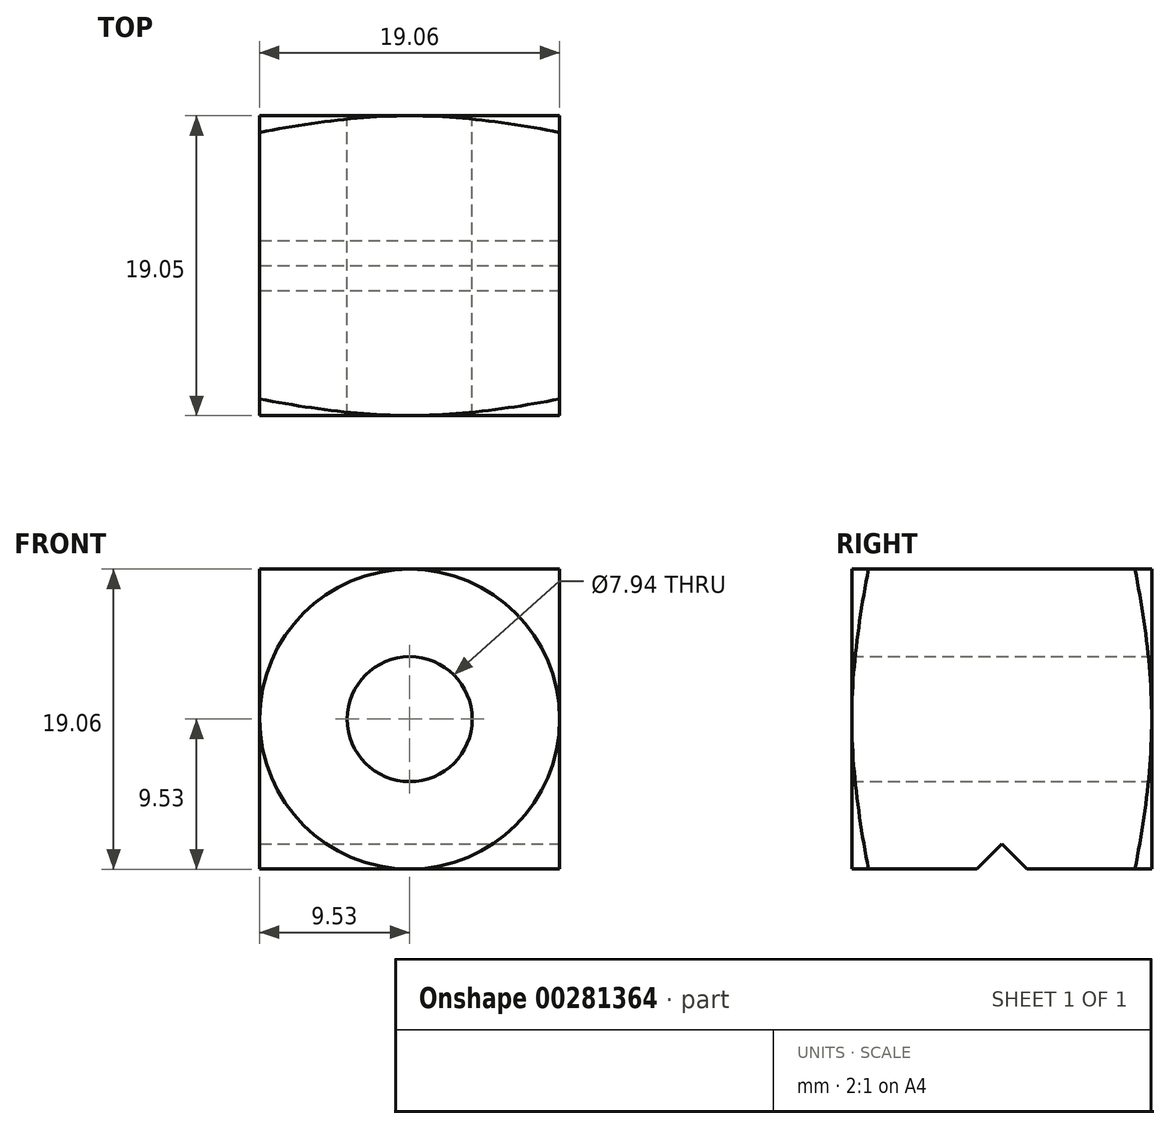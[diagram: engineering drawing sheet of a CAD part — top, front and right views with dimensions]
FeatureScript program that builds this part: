
annotation { "Feature Type Name" : "Feature", "Feature Type Description" : "" }
export const myFeature = defineFeature(function(context is Context, id is Id, definition is map)
    precondition{}
    {
        {
            var Q0;
            Q0=qCreatedBy(makeId("Front.planeOp"),FACE);
            var sketch = newSketch(context, id + "F0", { "sketchPlane" : qUnion([Q0])});
            skLineSegment(sketch, "E0.bottom", {"start": v(-9.52, -9.52) * mm, "end": v(9.52, -9.52) * mm});
            skLineSegment(sketch, "E0.top", {"start": v(-9.53, 9.52) * mm, "end": v(9.53, 9.52) * mm});
            skLineSegment(sketch, "E0.left", {"start": v(-9.53, -9.52) * mm, "end": v(-9.53, 9.52) * mm});
            skLineSegment(sketch, "E0.right", {"start": v(9.53, -9.52) * mm, "end": v(9.53, 9.52) * mm});
            skPoint(sketch, "E0.middle", {"position": v(0, 0) * mm});
            skCircle(sketch, "E1", {"center": v(0, 0) * mm, "radius": 3.97 * mm});
            skCircle(sketch, "E2", {"center": v(0, 0) * mm, "radius": 9.53 * mm});
            skSolve(sketch);
        }
        {
            var Q0;
            Q0 = qSketchRegion(id + "F0", true);
            extrude(context, id + "F1", {"entities" : qUnion([Q0]), "depth" : 19.05 * mm});
        }
        {
            var Q0;
            Q0=makeQuery(id+"F1.opExtrude","SWEPT_FACE",FACE,{"disambiguationData":[OSD([sQuery(id+"F0.wireOp",EDGE,"E0.right")])]});
            var sketch = newSketch(context, id + "F2", { "sketchPlane" : qUnion([Q0])});
            skLineSegment(sketch, "E3", {"start": v(-9.53, -7.94) * mm, "end": v(-11.11, -9.52) * mm});
            skPoint(sketch, "E3.startSnap0", {"position": v(-9.53, -9.52) * mm});
            skLineSegment(sketch, "E4", {"start": v(-9.53, -7.94) * mm, "end": v(-7.94, -9.52) * mm});
            skLineSegment(sketch, "E5", {"start": v(-9.53, -7.94) * mm, "end": v(-9.53, -15.34) * mm, "construction": true});
            skSolve(sketch);
        }
        {
            var Q0;
            Q0 = qSketchRegion(id + "F2", true);
            var Q1;
            {var subQ0=sQuery(id+"F2.wireOp",EDGE,"E3");Q1=makeQuery(id+"F2.imprint","IMPRINT",FACE,{"disambiguationData":[TD([[makeQuery(id+"F2.imprint","IMPRINT",EDGE,{"derivedFrom":subQ0}),1.0]])]});}
            extrude(context, id + "F3", {"entities" : qUnion([Q0, Q1]), "operationType" : NewBodyOperationType.REMOVE, "oppositeDirection" : true, "depth" : 19.05 * mm});
        }
        {
            var Q0;
            Q0=makeQuery(id+"F1.opExtrude","SWEPT_FACE",FACE,{"disambiguationData":[OSD([sQuery(id+"F0.wireOp",EDGE,"E0.right")])]});
            var Q1;
            Q1=makeQuery(id+"F1.opExtrude","SWEPT_FACE",FACE,{"disambiguationData":[OSD([sQuery(id+"F0.wireOp",EDGE,"E0.left")])]});
            cPlane(context, id + "F4", {"entities" : qUnion([Q0, Q1]), "cplaneType" : CPlaneType.MID_PLANE, "offset" : 25.4 * mm, "width" : 152.4 * mm, "height" : 152.4 * mm});
        }
        {
            var Q0;
            Q0=qCreatedBy(id+"F4.planeOp",FACE);
            var sketch = newSketch(context, id + "F5", { "sketchPlane" : qUnion([Q0])});
            skLineSegment(sketch, "E6.0.0", {"start": v(-11.11, -9.52) * mm, "end": v(-9.53, -7.94) * mm});
            skLineSegment(sketch, "E6.0.1", {"start": v(-9.53, -7.94) * mm, "end": v(-7.94, -9.52) * mm});
            skLineSegment(sketch, "E6.0.2", {"start": v(-7.94, -9.52) * mm, "end": v(0, -9.52) * mm});
            skLineSegment(sketch, "E6.0.3", {"start": v(0, -9.52) * mm, "end": v(0, 9.52) * mm});
            skLineSegment(sketch, "E6.0.4", {"start": v(0, 9.52) * mm, "end": v(-19.05, 9.52) * mm});
            skLineSegment(sketch, "E6.0.5", {"start": v(-19.05, 9.52) * mm, "end": v(-19.05, -9.52) * mm});
            skLineSegment(sketch, "E6.0.6", {"start": v(-19.05, -9.52) * mm, "end": v(-11.11, -9.52) * mm});
            skLineSegment(sketch, "E7", {"start": v(-19.05, 9.52) * mm, "end": v(-19.05, 20.54) * mm});
            skLineSegment(sketch, "E8", {"start": v(-19.05, 20.54) * mm, "end": v(-16.1, 20.54) * mm});
            skLineSegment(sketch, "E9", {"start": v(-16.1, 20.54) * mm, "end": v(-19.05, 9.52) * mm});
            skLineSegment(sketch, "E10", {"start": v(0, 9.52) * mm, "end": v(0, 20.54) * mm});
            skLineSegment(sketch, "E11", {"start": v(0, 20.54) * mm, "end": v(-2.95, 20.54) * mm});
            skLineSegment(sketch, "E12", {"start": v(-2.95, 20.54) * mm, "end": v(0, 9.53) * mm});
            skSolve(sketch);
        }
        {
            var Q0;
            Q0=makeQuery(id+"F5.imprint","IMPRINT",FACE,{"disambiguationData":[TD([[makeQuery(id+"F5.imprint","IMPRINT",EDGE,{"derivedFrom":sQuery(id+"F5.wireOp",EDGE,"E7")}),-1.0]])]});
            var Q1;
            Q1=makeQuery(id+"F5.imprint","IMPRINT",FACE,{"disambiguationData":[TD([[makeQuery(id+"F5.imprint","IMPRINT",EDGE,{"derivedFrom":sQuery(id+"F5.wireOp",EDGE,"E10")}),1.0]])]});
            var Q2;
            Q2=makeQuery(id+"F1.opExtrude","SWEPT_FACE",FACE,{"disambiguationData":[OSD([sQuery(id+"F0.wireOp",EDGE,"E1")])]});
            revolve(context, id + "F6", {"operationType" : NewBodyOperationType.REMOVE, "entities" : qUnion([Q0, Q1]), "axis" : qUnion([Q2]), "revolveType" : RevolveType.FULL, "oppositeDirection" : true});
        }
    });
